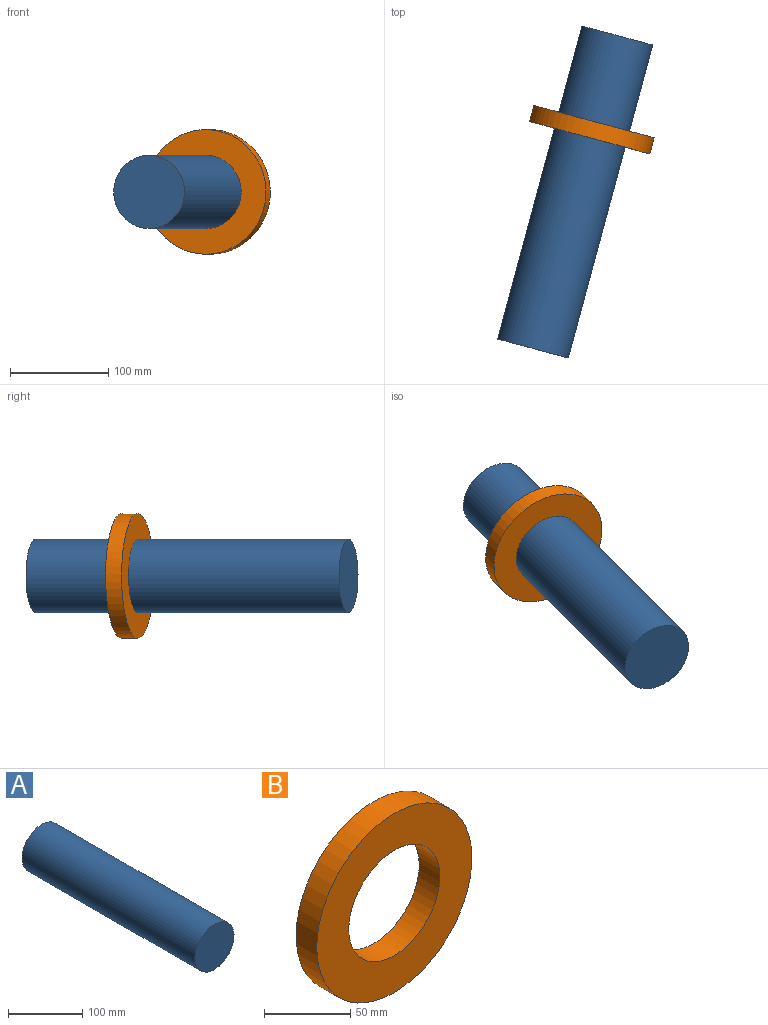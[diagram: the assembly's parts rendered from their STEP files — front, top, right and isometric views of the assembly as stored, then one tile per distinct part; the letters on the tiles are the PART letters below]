
ASSEMBLY  parts=2 mates=1
PART A: 3 faces, bbox 74.6x330.2x74.6 mm
  f0: cylinder r=37.31mm len=330.2mm, axis (0,1,0), area 77399.6mm2, adj f1,f2
  f1: plane 74.61x74.61mm, normal (0,-1,0), area 4372.3mm2, adj f0
  f2: plane 74.61x74.61mm, normal (0,1,0), area 4372.3mm2, adj f0
PART B: 4 faces, bbox 127x16.9x127 mm
  f0: cylinder r=37.31mm len=74.61mm, axis (0,1,0), area 3959.3mm2, adj f2,f3
  f1: cylinder r=63.5mm len=127mm, axis (0,1,0), area 6739.2mm2, adj f2,f3
  f2: plane 127x127mm, normal (0,-1,0), area 8295.4mm2, adj f0,f1
  f3: plane 127x127mm, normal (0,1,0), area 8295.4mm2, adj f0,f1
PLACE A rot(axis=(0,0,-1),15deg) t=(300.52,-12.77,85.09)mm
PLACE B rot(axis=(0,0,-1),15deg) t=(356.03,193.72,85.09)mm
MATE slider B.f1 <-> A.f0  axis (0.26,0.97,0) through (356.03,193.72,85.09)mm
